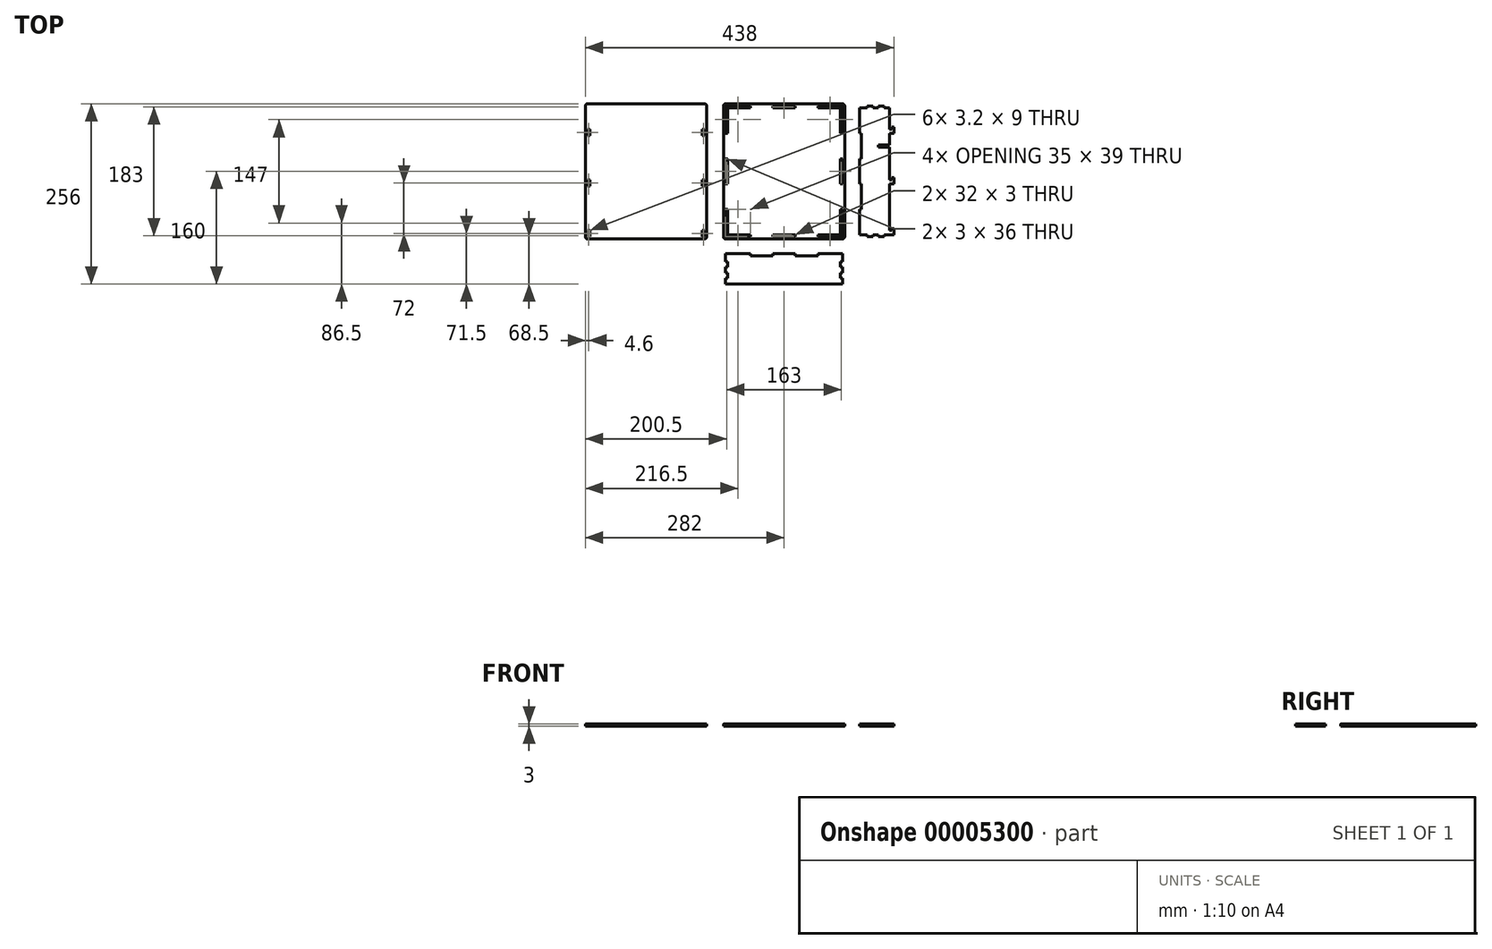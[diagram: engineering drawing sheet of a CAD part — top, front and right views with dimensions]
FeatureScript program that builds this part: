
annotation { "Feature Type Name" : "Feature", "Feature Type Description" : "" }
export const myFeature = defineFeature(function(context is Context, id is Id, definition is map)
    precondition{}
    {
        {
            assignVariable(context, id + "F0", {"name" : "MaterialThickness", "anyValue" : 3});
        }
        {
            var Q0;
            Q0=qCreatedBy(makeId("Top.planeOp"),FACE);
            var sketch = newSketch(context, id + "F1", { "sketchPlane" : qUnion([Q0])});
            skLineSegment(sketch, "E0", {"start": v(0, 0) * mm, "end": v(160, 0) * mm});
            skLineSegment(sketch, "E1", {"start": v(160, 0) * mm, "end": v(160, 180) * mm});
            skLineSegment(sketch, "E2", {"start": v(160, 180) * mm, "end": v(0, 180) * mm});
            skLineSegment(sketch, "E3", {"start": v(0, 180) * mm, "end": v(0, 0) * mm});
            skLineSegment(sketch, "E4", {"start": v(64, 183) * mm, "end": v(64, 180) * mm});
            skLineSegment(sketch, "E5", {"start": v(96, 180) * mm, "end": v(96, 183) * mm});
            skLineSegment(sketch, "E6", {"start": v(96, 183) * mm, "end": v(128, 183) * mm});
            skLineSegment(sketch, "E7", {"start": v(128, 183) * mm, "end": v(128, 180) * mm});
            skLineSegment(sketch, "E8", {"start": v(64, 183) * mm, "end": v(32, 183) * mm});
            skLineSegment(sketch, "E9", {"start": v(32, 183) * mm, "end": v(32, 180) * mm});
            skLineSegment(sketch, "E10", {"start": v(0, 90) * mm, "end": v(160, 90) * mm, "construction": true});
            skLineSegment(sketch, "E11.MirrorCS", {"start": v(64, -3) * mm, "end": v(64, 0) * mm});
            skLineSegment(sketch, "E12.MirrorCS", {"start": v(128, -3) * mm, "end": v(128, 0) * mm});
            skLineSegment(sketch, "E13.MirrorCS", {"start": v(32, -3) * mm, "end": v(32, 0) * mm});
            skLineSegment(sketch, "E14.MirrorCS", {"start": v(64, -3) * mm, "end": v(32, -3) * mm});
            skLineSegment(sketch, "E15.MirrorCS", {"start": v(96, 0) * mm, "end": v(96, -3) * mm});
            skLineSegment(sketch, "E16.MirrorCS", {"start": v(96, -3) * mm, "end": v(128, -3) * mm});
            skLineSegment(sketch, "E17", {"start": v(0, 144) * mm, "end": v(-3, 144) * mm});
            skLineSegment(sketch, "E18", {"start": v(-3, 144) * mm, "end": v(-3, 108) * mm});
            skLineSegment(sketch, "E19", {"start": v(-3, 108) * mm, "end": v(0, 108) * mm});
            skLineSegment(sketch, "E20", {"start": v(0, 72) * mm, "end": v(-3, 72) * mm});
            skLineSegment(sketch, "E21", {"start": v(-3, 72) * mm, "end": v(-3, 36) * mm});
            skLineSegment(sketch, "E22", {"start": v(-3, 36) * mm, "end": v(0, 36) * mm});
            skLineSegment(sketch, "E23", {"start": v(80, 180) * mm, "end": v(80, 0) * mm, "construction": true});
            skLineSegment(sketch, "E24.MirrorCS", {"start": v(163, 144) * mm, "end": v(163, 108) * mm});
            skLineSegment(sketch, "E25.MirrorCS", {"start": v(163, 108) * mm, "end": v(160, 108) * mm});
            skLineSegment(sketch, "E26.MirrorCS", {"start": v(163, 36) * mm, "end": v(160, 36) * mm});
            skLineSegment(sketch, "E27.MirrorCS", {"start": v(163, 72) * mm, "end": v(163, 36) * mm});
            skLineSegment(sketch, "E28.MirrorCS", {"start": v(160, 144) * mm, "end": v(163, 144) * mm});
            skLineSegment(sketch, "E29.MirrorCS", {"start": v(160, 72) * mm, "end": v(163, 72) * mm});
            skLineSegment(sketch, "E30", {"start": v(0, -30) * mm, "end": v(160, -30) * mm});
            skLineSegment(sketch, "E31", {"start": v(160, -30) * mm, "end": v(160, -70) * mm});
            skLineSegment(sketch, "E32", {"start": v(160, -70) * mm, "end": v(0, -70) * mm});
            skLineSegment(sketch, "E33", {"start": v(0, -70) * mm, "end": v(0, -30) * mm});
            skLineSegment(sketch, "E34", {"start": v(0, -30) * mm, "end": v(0, -27) * mm});
            skLineSegment(sketch, "E35", {"start": v(0, -27) * mm, "end": v(32, -27) * mm});
            skLineSegment(sketch, "E36", {"start": v(32, -27) * mm, "end": v(32, -30) * mm});
            skLineSegment(sketch, "E37", {"start": v(64, -30) * mm, "end": v(64, -27) * mm});
            skLineSegment(sketch, "E38", {"start": v(64, -27) * mm, "end": v(96, -27) * mm});
            skLineSegment(sketch, "E39", {"start": v(96, -27) * mm, "end": v(96, -30) * mm});
            skLineSegment(sketch, "E40", {"start": v(128, -30) * mm, "end": v(128, -27) * mm});
            skLineSegment(sketch, "E41", {"start": v(128, -27) * mm, "end": v(160, -27) * mm});
            skLineSegment(sketch, "E42", {"start": v(160, -27) * mm, "end": v(160, -30) * mm});
            skLineSegment(sketch, "E43", {"start": v(0, -27) * mm, "end": v(-3, -27) * mm});
            skLineSegment(sketch, "E44", {"start": v(-3, -27) * mm, "end": v(-3, -38) * mm});
            skLineSegment(sketch, "E45", {"start": v(-3, -38) * mm, "end": v(0, -38) * mm});
            skLineSegment(sketch, "E46", {"start": v(0, -46) * mm, "end": v(-3, -46) * mm});
            skLineSegment(sketch, "E47", {"start": v(-3, -46) * mm, "end": v(-3, -54) * mm});
            skLineSegment(sketch, "E48", {"start": v(-3, -54) * mm, "end": v(0, -54) * mm});
            skLineSegment(sketch, "E49", {"start": v(0, -70) * mm, "end": v(-3, -70) * mm});
            skLineSegment(sketch, "E50", {"start": v(-3, -70) * mm, "end": v(-3, -62) * mm});
            skLineSegment(sketch, "E51", {"start": v(-3, -62) * mm, "end": v(0, -62) * mm});
            skLineSegment(sketch, "E52", {"start": v(80, -30) * mm, "end": v(80, -70) * mm, "construction": true});
            skLineSegment(sketch, "E53.MirrorCS", {"start": v(160, -27) * mm, "end": v(163, -27) * mm});
            skLineSegment(sketch, "E54.MirrorCS", {"start": v(160, -70) * mm, "end": v(163, -70) * mm});
            skLineSegment(sketch, "E55.MirrorCS", {"start": v(160, -46) * mm, "end": v(163, -46) * mm});
            skLineSegment(sketch, "E56.MirrorCS", {"start": v(163, -38) * mm, "end": v(160, -38) * mm});
            skLineSegment(sketch, "E57.MirrorCS", {"start": v(163, -54) * mm, "end": v(160, -54) * mm});
            skLineSegment(sketch, "E58.MirrorCS", {"start": v(163, -62) * mm, "end": v(160, -62) * mm});
            skLineSegment(sketch, "E59.MirrorCS", {"start": v(163, -27) * mm, "end": v(163, -38) * mm});
            skLineSegment(sketch, "E60.MirrorCS", {"start": v(163, -46) * mm, "end": v(163, -54) * mm});
            skLineSegment(sketch, "E61.MirrorCS", {"start": v(163, -70) * mm, "end": v(163, -62) * mm});
            skLineSegment(sketch, "E62", {"start": v(190, 0) * mm, "end": v(190, 180) * mm});
            skLineSegment(sketch, "E63", {"start": v(190, 180) * mm, "end": v(230, 180) * mm});
            skLineSegment(sketch, "E64", {"start": v(230, 180) * mm, "end": v(230, 0) * mm});
            skLineSegment(sketch, "E65", {"start": v(230, 0) * mm, "end": v(190, 0) * mm});
            skLineSegment(sketch, "E66", {"start": v(198, 0) * mm, "end": v(198, -3) * mm});
            skLineSegment(sketch, "E67", {"start": v(198, -3) * mm, "end": v(206, -3) * mm});
            skLineSegment(sketch, "E68", {"start": v(206, -3) * mm, "end": v(206, 0) * mm});
            skLineSegment(sketch, "E69", {"start": v(214, 0) * mm, "end": v(214, -3) * mm});
            skLineSegment(sketch, "E70", {"start": v(214, -3) * mm, "end": v(222, -3) * mm});
            skLineSegment(sketch, "E71", {"start": v(222, -3) * mm, "end": v(222, 0) * mm});
            skLineSegment(sketch, "E72", {"start": v(190, 0) * mm, "end": v(187, 0) * mm});
            skLineSegment(sketch, "E73", {"start": v(187, 0) * mm, "end": v(187, 36) * mm});
            skLineSegment(sketch, "E74", {"start": v(187, 36) * mm, "end": v(190, 36) * mm});
            skLineSegment(sketch, "E75", {"start": v(190, 72) * mm, "end": v(187, 72) * mm});
            skLineSegment(sketch, "E76", {"start": v(187, 72) * mm, "end": v(187, 108) * mm});
            skLineSegment(sketch, "E77", {"start": v(187, 108) * mm, "end": v(190, 108) * mm});
            skLineSegment(sketch, "E78", {"start": v(190, 144) * mm, "end": v(187, 144) * mm});
            skLineSegment(sketch, "E79", {"start": v(187, 144) * mm, "end": v(187, 180) * mm});
            skLineSegment(sketch, "E80", {"start": v(187, 180) * mm, "end": v(190, 180) * mm});
            skLineSegment(sketch, "E81", {"start": v(190, 90) * mm, "end": v(230, 90) * mm, "construction": true});
            skLineSegment(sketch, "E82.MirrorCS", {"start": v(214, 180) * mm, "end": v(214, 183) * mm});
            skLineSegment(sketch, "E83.MirrorCS", {"start": v(222, 183) * mm, "end": v(222, 180) * mm});
            skLineSegment(sketch, "E84.MirrorCS", {"start": v(206, 183) * mm, "end": v(206, 180) * mm});
            skLineSegment(sketch, "E85.MirrorCS", {"start": v(198, 180) * mm, "end": v(198, 183) * mm});
            skLineSegment(sketch, "E86.MirrorCS", {"start": v(198, 183) * mm, "end": v(206, 183) * mm});
            skLineSegment(sketch, "E87.MirrorCS", {"start": v(214, 183) * mm, "end": v(222, 183) * mm});
            skLineSegment(sketch, "E88", {"start": v(230, 0) * mm, "end": v(236, 0) * mm});
            skLineSegment(sketch, "E89", {"start": v(236, 0) * mm, "end": v(236, 9) * mm});
            skLineSegment(sketch, "E90", {"start": v(236, 9) * mm, "end": v(233, 9) * mm});
            skLineSegment(sketch, "E91", {"start": v(233, 9) * mm, "end": v(233, 6) * mm});
            skLineSegment(sketch, "E92", {"start": v(233, 6) * mm, "end": v(230, 6) * mm});
            skLineSegment(sketch, "E93", {"start": v(230, 72) * mm, "end": v(236, 72) * mm});
            skLineSegment(sketch, "E94", {"start": v(236, 72) * mm, "end": v(236, 81) * mm});
            skLineSegment(sketch, "E95", {"start": v(236, 81) * mm, "end": v(233, 81) * mm});
            skLineSegment(sketch, "E96", {"start": v(233, 81) * mm, "end": v(233, 78) * mm});
            skLineSegment(sketch, "E97", {"start": v(233, 78) * mm, "end": v(230, 78) * mm});
            skLineSegment(sketch, "E98", {"start": v(230, 144) * mm, "end": v(236, 144) * mm});
            skLineSegment(sketch, "E99", {"start": v(236, 144) * mm, "end": v(236, 153) * mm});
            skLineSegment(sketch, "E100", {"start": v(236, 153) * mm, "end": v(233, 153) * mm});
            skLineSegment(sketch, "E101", {"start": v(233, 153) * mm, "end": v(233, 150) * mm});
            skLineSegment(sketch, "E102", {"start": v(233, 150) * mm, "end": v(230, 150) * mm});
            skLineSegment(sketch, "E103", {"start": v(-30, -6) * mm, "end": v(-30, 186) * mm});
            skLineSegment(sketch, "E104", {"start": v(-30, 186) * mm, "end": v(-202, 186) * mm});
            skLineSegment(sketch, "E105", {"start": v(-202, 186) * mm, "end": v(-202, -6) * mm});
            skLineSegment(sketch, "E106", {"start": v(-202, -6) * mm, "end": v(-30, -6) * mm});
            skLineSegment(sketch, "E107", {"start": v(-33, 6) * mm, "end": v(-36.2, 6) * mm});
            skLineSegment(sketch, "E108", {"start": v(-36.2, 6) * mm, "end": v(-36.2, -3) * mm});
            skLineSegment(sketch, "E109", {"start": v(-36.2, -3) * mm, "end": v(-33, -3) * mm});
            skLineSegment(sketch, "E110", {"start": v(-33, -3) * mm, "end": v(-33, 6) * mm});
            skLineSegment(sketch, "E111", {"start": v(-33, 78) * mm, "end": v(-36.2, 78) * mm});
            skLineSegment(sketch, "E112", {"start": v(-36.2, 78) * mm, "end": v(-36.2, 69) * mm});
            skLineSegment(sketch, "E113", {"start": v(-36.2, 69) * mm, "end": v(-33, 69) * mm});
            skLineSegment(sketch, "E114", {"start": v(-33, 69) * mm, "end": v(-33, 78) * mm});
            skLineSegment(sketch, "E115", {"start": v(-116, -6) * mm, "end": v(-116, 186) * mm, "construction": true});
            skLineSegment(sketch, "E116", {"start": v(-33, 150) * mm, "end": v(-36.2, 150) * mm});
            skLineSegment(sketch, "E117", {"start": v(-36.2, 150) * mm, "end": v(-36.2, 141) * mm});
            skLineSegment(sketch, "E118", {"start": v(-36.2, 141) * mm, "end": v(-33, 141) * mm});
            skLineSegment(sketch, "E119", {"start": v(-33, 141) * mm, "end": v(-33, 150) * mm});
            skLineSegment(sketch, "E120.MirrorCS", {"start": v(-195.8, 69) * mm, "end": v(-199, 69) * mm});
            skLineSegment(sketch, "E121.MirrorCS", {"start": v(-199, 69) * mm, "end": v(-199, 78) * mm});
            skLineSegment(sketch, "E122.MirrorCS", {"start": v(-199, 6) * mm, "end": v(-195.8, 6) * mm});
            skLineSegment(sketch, "E123.MirrorCS", {"start": v(-195.8, 78) * mm, "end": v(-195.8, 69) * mm});
            skLineSegment(sketch, "E124.MirrorCS", {"start": v(-195.8, -3) * mm, "end": v(-199, -3) * mm});
            skLineSegment(sketch, "E125.MirrorCS", {"start": v(-195.8, 6) * mm, "end": v(-195.8, -3) * mm});
            skLineSegment(sketch, "E126.MirrorCS", {"start": v(-199, 78) * mm, "end": v(-195.8, 78) * mm});
            skLineSegment(sketch, "E127.MirrorCS", {"start": v(-199, 150) * mm, "end": v(-195.8, 150) * mm});
            skLineSegment(sketch, "E128.MirrorCS", {"start": v(-199, -3) * mm, "end": v(-199, 6) * mm});
            skLineSegment(sketch, "E129.MirrorCS", {"start": v(-195.8, 150) * mm, "end": v(-195.8, 141) * mm});
            skLineSegment(sketch, "E130.MirrorCS", {"start": v(-199, 141) * mm, "end": v(-199, 150) * mm});
            skLineSegment(sketch, "E131.MirrorCS", {"start": v(-195.8, 141) * mm, "end": v(-199, 141) * mm});
            skLineSegment(sketch, "E132", {"start": v(230, 127.5) * mm, "end": v(214, 127.5) * mm});
            skLineSegment(sketch, "E133", {"start": v(214, 127.5) * mm, "end": v(214, 124.5) * mm});
            skLineSegment(sketch, "E134", {"start": v(214, 124.5) * mm, "end": v(230, 124.5) * mm});
            skLineSegment(sketch, "E135", {"start": v(214, 126) * mm, "end": v(230, 126) * mm, "construction": true});
            skPoint(sketch, "E136", {"position": v(187, 18) * mm});
            skLineSegment(sketch, "E137", {"start": v(-6, 186) * mm, "end": v(-6, -6) * mm});
            skLineSegment(sketch, "E138", {"start": v(-6, -6) * mm, "end": v(166, -6) * mm});
            skLineSegment(sketch, "E139", {"start": v(166, -6) * mm, "end": v(166, 186) * mm});
            skLineSegment(sketch, "E140", {"start": v(166, 186) * mm, "end": v(-6, 186) * mm});
            skLineSegment(sketch, "E141", {"start": v(-3, 144) * mm, "end": v(-3, 183) * mm});
            skLineSegment(sketch, "E142", {"start": v(-3, 183) * mm, "end": v(32, 183) * mm});
            skLineSegment(sketch, "E143.MirrorCS", {"start": v(163, 183) * mm, "end": v(128, 183) * mm});
            skLineSegment(sketch, "E144.MirrorCS", {"start": v(163, 144) * mm, "end": v(163, 183) * mm});
            skLineSegment(sketch, "E145.MirrorCS", {"start": v(163, 36) * mm, "end": v(163, -3) * mm});
            skLineSegment(sketch, "E146.MirrorCS", {"start": v(163, -3) * mm, "end": v(128, -3) * mm});
            skLineSegment(sketch, "E147.MirrorCS", {"start": v(-3, 36) * mm, "end": v(-3, -3) * mm});
            skLineSegment(sketch, "E148.MirrorCS", {"start": v(-3, -3) * mm, "end": v(32, -3) * mm});
            skLineSegment(sketch, "E149", {"start": v(64, 183) * mm, "end": v(96, 183) * mm});
            skLineSegment(sketch, "E150.MirrorCS", {"start": v(64, -3) * mm, "end": v(96, -3) * mm});
            skLineSegment(sketch, "E151", {"start": v(-3, 108) * mm, "end": v(-3, 72) * mm});
            skLineSegment(sketch, "E152.MirrorCS", {"start": v(163, 108) * mm, "end": v(163, 72) * mm});
            skSolve(sketch);
        }
        {
            var Q0;
            Q0=makeQuery(id+"F1.imprint","IMPRINT",FACE,{"disambiguationData":[TD([[makeQuery(id+"F1.imprint","IMPRINT",EDGE,{"derivedFrom":sQuery(id+"F1.wireOp",EDGE,"E103")}),1.0]])]});
            var Q1;
            {var subQ15=sQuery(id+"F1.wireOp",EDGE,"E32");Q1=makeQuery(id+"F1.imprint","IMPRINT",FACE,{"disambiguationData":[TD([[makeQuery(id+"F1.imprint","IMPRINT",EDGE,{"derivedFrom":subQ15}),-1.0]])]});}
            var Q2;
            {var subQ0=sQuery(id+"F1.wireOp",EDGE,"E34");Q2=makeQuery(id+"F1.imprint","IMPRINT",FACE,{"disambiguationData":[TD([[makeQuery(id+"F1.imprint","IMPRINT",EDGE,{"derivedFrom":subQ0}),-1.0]])]});}
            var Q3;
            {var subQ5=sQuery(id+"F1.wireOp",EDGE,"E62");var subQ7=makeQuery(id+"F1.imprint","INTERSECT",VERTEX,{"derivedFrom":[subQ5,sQuery(id+"F1.wireOp",EDGE,"E74")]});Q3=makeQuery(id+"F1.imprint","IMPRINT",FACE,{"disambiguationData":[TD([[makeQuery(id+"F1.imprint","IMPRINT",EDGE,{"disambiguationData":[TD([[subQ7,-1.0]])],"derivedFrom":subQ5}),-1.0]])]});}
            var Q4;
            {var subQ0=sQuery(id+"F1.wireOp",EDGE,"E69");Q4=makeQuery(id+"F1.imprint","IMPRINT",FACE,{"disambiguationData":[TD([[makeQuery(id+"F1.imprint","IMPRINT",EDGE,{"derivedFrom":subQ0}),1.0]])]});}
            var Q5;
            {var subQ2=sQuery(id+"F1.wireOp",EDGE,"E40");Q5=makeQuery(id+"F1.imprint","IMPRINT",FACE,{"disambiguationData":[TD([[makeQuery(id+"F1.imprint","IMPRINT",EDGE,{"derivedFrom":subQ2}),-1.0]])]});}
            var Q6;
            {var subQ0=sQuery(id+"F1.wireOp",EDGE,"E66");Q6=makeQuery(id+"F1.imprint","IMPRINT",FACE,{"disambiguationData":[TD([[makeQuery(id+"F1.imprint","IMPRINT",EDGE,{"derivedFrom":subQ0}),1.0]])]});}
            var Q7;
            {var subQ2=sQuery(id+"F1.wireOp",EDGE,"E78");Q7=makeQuery(id+"F1.imprint","IMPRINT",FACE,{"disambiguationData":[TD([[makeQuery(id+"F1.imprint","IMPRINT",EDGE,{"derivedFrom":subQ2}),-1.0]])]});}
            var Q8;
            {var subQ0=sQuery(id+"F1.wireOp",EDGE,"E72");Q8=makeQuery(id+"F1.imprint","IMPRINT",FACE,{"disambiguationData":[TD([[makeQuery(id+"F1.imprint","IMPRINT",EDGE,{"derivedFrom":subQ0}),-1.0]])]});}
            var Q9;
            {var subQ0=sQuery(id+"F1.wireOp",EDGE,"E84.MirrorCS");Q9=makeQuery(id+"F1.imprint","IMPRINT",FACE,{"disambiguationData":[TD([[makeQuery(id+"F1.imprint","IMPRINT",EDGE,{"derivedFrom":subQ0}),-1.0]])]});}
            var Q10;
            {var subQ0=sQuery(id+"F1.wireOp",EDGE,"E34");Q10=makeQuery(id+"F1.imprint","IMPRINT",FACE,{"disambiguationData":[TD([[makeQuery(id+"F1.imprint","IMPRINT",EDGE,{"derivedFrom":subQ0}),1.0]])]});}
            var Q11;
            {var subQ0=sQuery(id+"F1.wireOp",EDGE,"E11.MirrorCS");Q11=makeQuery(id+"F1.imprint","IMPRINT",FACE,{"disambiguationData":[TD([[makeQuery(id+"F1.imprint","IMPRINT",EDGE,{"derivedFrom":subQ0}),1.0]])]});}
            var Q12;
            {var subQ0=sQuery(id+"F1.wireOp",EDGE,"E12.MirrorCS");Q12=makeQuery(id+"F1.imprint","IMPRINT",FACE,{"disambiguationData":[TD([[makeQuery(id+"F1.imprint","IMPRINT",EDGE,{"derivedFrom":subQ0}),1.0]])]});}
            var Q13;
            {var subQ0=sQuery(id+"F1.wireOp",EDGE,"E26.MirrorCS");Q13=makeQuery(id+"F1.imprint","IMPRINT",FACE,{"disambiguationData":[TD([[makeQuery(id+"F1.imprint","IMPRINT",EDGE,{"derivedFrom":subQ0}),-1.0]])]});}
            var Q14;
            Q14=makeQuery(id+"F1.imprint","IMPRINT",FACE,{"disambiguationData":[TD([[makeQuery(id+"F1.imprint","IMPRINT",EDGE,{"derivedFrom":sQuery(id+"F1.wireOp",EDGE,"E24.MirrorCS")}),-1.0]])]});
            var Q15;
            {var subQ0=sQuery(id+"F1.wireOp",EDGE,"E5");Q15=makeQuery(id+"F1.imprint","IMPRINT",FACE,{"disambiguationData":[TD([[makeQuery(id+"F1.imprint","IMPRINT",EDGE,{"derivedFrom":subQ0}),-1.0]])]});}
            var Q16;
            {var subQ0=sQuery(id+"F1.wireOp",EDGE,"E4");Q16=makeQuery(id+"F1.imprint","IMPRINT",FACE,{"disambiguationData":[TD([[makeQuery(id+"F1.imprint","IMPRINT",EDGE,{"derivedFrom":subQ0}),-1.0]])]});}
            var Q17;
            {var subQ0=sQuery(id+"F1.wireOp",EDGE,"E17");Q17=makeQuery(id+"F1.imprint","IMPRINT",FACE,{"disambiguationData":[TD([[makeQuery(id+"F1.imprint","IMPRINT",EDGE,{"derivedFrom":subQ0}),1.0]])]});}
            var Q18;
            {var subQ0=sQuery(id+"F1.wireOp",EDGE,"E20");Q18=makeQuery(id+"F1.imprint","IMPRINT",FACE,{"disambiguationData":[TD([[makeQuery(id+"F1.imprint","IMPRINT",EDGE,{"derivedFrom":subQ0}),1.0]])]});}
            var Q19;
            {var subQ0=sQuery(id+"F1.wireOp",EDGE,"E37");Q19=makeQuery(id+"F1.imprint","IMPRINT",FACE,{"disambiguationData":[TD([[makeQuery(id+"F1.imprint","IMPRINT",EDGE,{"derivedFrom":subQ0}),-1.0]])]});}
            var Q20;
            {var subQ0=sQuery(id+"F1.wireOp",EDGE,"E55.MirrorCS");Q20=makeQuery(id+"F1.imprint","IMPRINT",FACE,{"disambiguationData":[TD([[makeQuery(id+"F1.imprint","IMPRINT",EDGE,{"derivedFrom":subQ0}),-1.0]])]});}
            var Q21;
            {var subQ0=sQuery(id+"F1.wireOp",EDGE,"E54.MirrorCS");Q21=makeQuery(id+"F1.imprint","IMPRINT",FACE,{"disambiguationData":[TD([[makeQuery(id+"F1.imprint","IMPRINT",EDGE,{"derivedFrom":subQ0}),1.0]])]});}
            var Q22;
            {var subQ0=sQuery(id+"F1.wireOp",EDGE,"E49");Q22=makeQuery(id+"F1.imprint","IMPRINT",FACE,{"disambiguationData":[TD([[makeQuery(id+"F1.imprint","IMPRINT",EDGE,{"derivedFrom":subQ0}),-1.0]])]});}
            var Q23;
            {var subQ0=sQuery(id+"F1.wireOp",EDGE,"E46");Q23=makeQuery(id+"F1.imprint","IMPRINT",FACE,{"disambiguationData":[TD([[makeQuery(id+"F1.imprint","IMPRINT",EDGE,{"derivedFrom":subQ0}),1.0]])]});}
            var Q24;
            {var subQ0=sQuery(id+"F1.wireOp",EDGE,"E82.MirrorCS");Q24=makeQuery(id+"F1.imprint","IMPRINT",FACE,{"disambiguationData":[TD([[makeQuery(id+"F1.imprint","IMPRINT",EDGE,{"derivedFrom":subQ0}),-1.0]])]});}
            var Q25;
            {var subQ3=sQuery(id+"F1.wireOp",EDGE,"E3");var subQ4=sQuery(id+"F1.wireOp",EDGE,"E0");var subQ5=makeQuery(id+"F1.imprint","INTERSECT",VERTEX,{"derivedFrom":[subQ4,subQ3]});Q25=makeQuery(id+"F1.imprint","IMPRINT",FACE,{"disambiguationData":[TD([[makeQuery(id+"F1.imprint","IMPRINT",EDGE,{"disambiguationData":[TD([[subQ5,-1.0]])],"derivedFrom":subQ4}),1.0]])]});}
            var Q26;
            {var subQ0=sQuery(id+"F1.wireOp",EDGE,"E42");Q26=makeQuery(id+"F1.imprint","IMPRINT",FACE,{"disambiguationData":[TD([[makeQuery(id+"F1.imprint","IMPRINT",EDGE,{"derivedFrom":subQ0}),1.0]])]});}
            var Q27;
            {var subQ0=sQuery(id+"F1.wireOp",EDGE,"E88");Q27=makeQuery(id+"F1.imprint","IMPRINT",FACE,{"disambiguationData":[TD([[makeQuery(id+"F1.imprint","IMPRINT",EDGE,{"derivedFrom":subQ0}),1.0]])]});}
            var Q28;
            {var subQ0=sQuery(id+"F1.wireOp",EDGE,"E75");Q28=makeQuery(id+"F1.imprint","IMPRINT",FACE,{"disambiguationData":[TD([[makeQuery(id+"F1.imprint","IMPRINT",EDGE,{"derivedFrom":subQ0}),-1.0]])]});}
            var Q29;
            {var subQ0=sQuery(id+"F1.wireOp",EDGE,"E98");Q29=makeQuery(id+"F1.imprint","IMPRINT",FACE,{"disambiguationData":[TD([[makeQuery(id+"F1.imprint","IMPRINT",EDGE,{"derivedFrom":subQ0}),1.0]])]});}
            var Q30;
            {var subQ0=sQuery(id+"F1.wireOp",EDGE,"E93");Q30=makeQuery(id+"F1.imprint","IMPRINT",FACE,{"disambiguationData":[TD([[makeQuery(id+"F1.imprint","IMPRINT",EDGE,{"derivedFrom":subQ0}),1.0]])]});}
            var Q31;
            Q31=makeQuery(id+"F1.imprint","IMPRINT",FACE,{"disambiguationData":[TD([[makeQuery(id+"F1.imprint","IMPRINT",EDGE,{"derivedFrom":sQuery(id+"F1.wireOp",EDGE,"E6")}),1.0]])]});
            extrude(context, id + "F2", {"entities" : qUnion([Q0, Q1, Q2, Q3, Q4, Q5, Q6, Q7, Q8, Q9, Q10, Q11, Q12, Q13, Q14, Q15, Q16, Q17, Q18, Q19, Q20, Q21, Q22, Q23, Q24, Q25, Q26, Q27, Q28, Q29, Q30, Q31]), "depth" : (getVariable(context, 'MaterialThickness')) * mm});
        }
        {
            var Q0;
            Q0=makeQuery(id+"F2.opExtrude","SWEPT_EDGE",EDGE,{"disambiguationData":[OSD([sQuery(id+"F1.wireOp",EDGE,"E103"),sQuery(id+"F1.wireOp",EDGE,"E106")])]});
            var Q1;
            Q1=makeQuery(id+"F2.opExtrude","SWEPT_EDGE",EDGE,{"disambiguationData":[OSD([sQuery(id+"F1.wireOp",EDGE,"E105"),sQuery(id+"F1.wireOp",EDGE,"E106")])]});
            var Q2;
            Q2=makeQuery(id+"F2.opExtrude","SWEPT_EDGE",EDGE,{"disambiguationData":[OSD([sQuery(id+"F1.wireOp",EDGE,"E104"),sQuery(id+"F1.wireOp",EDGE,"E105")])]});
            var Q3;
            Q3=makeQuery(id+"F2.opExtrude","SWEPT_EDGE",EDGE,{"disambiguationData":[OSD([sQuery(id+"F1.wireOp",EDGE,"E103"),sQuery(id+"F1.wireOp",EDGE,"E104")])]});
            var Q4;
            Q4=makeQuery(id+"F2.opExtrude","SWEPT_EDGE",EDGE,{"disambiguationData":[OSD([sQuery(id+"F1.wireOp",EDGE,"E137"),sQuery(id+"F1.wireOp",EDGE,"E138")])]});
            var Q5;
            Q5=makeQuery(id+"F2.opExtrude","SWEPT_EDGE",EDGE,{"disambiguationData":[OSD([sQuery(id+"F1.wireOp",EDGE,"E138"),sQuery(id+"F1.wireOp",EDGE,"E139")])]});
            var Q6;
            Q6=makeQuery(id+"F2.opExtrude","SWEPT_EDGE",EDGE,{"disambiguationData":[OSD([sQuery(id+"F1.wireOp",EDGE,"E139"),sQuery(id+"F1.wireOp",EDGE,"E140")])]});
            var Q7;
            Q7=makeQuery(id+"F2.opExtrude","SWEPT_EDGE",EDGE,{"disambiguationData":[OSD([sQuery(id+"F1.wireOp",EDGE,"E137"),sQuery(id+"F1.wireOp",EDGE,"E140")])]});
            fillet(context, id + "F3", {"entities" : qUnion([Q0, Q1, Q2, Q3, Q4, Q5, Q6, Q7]), "radius" : (getVariable(context, 'MaterialThickness')) * mm, "tangentPropagation" : true, "allowEdgeOverflow" : false});
        }
    });
